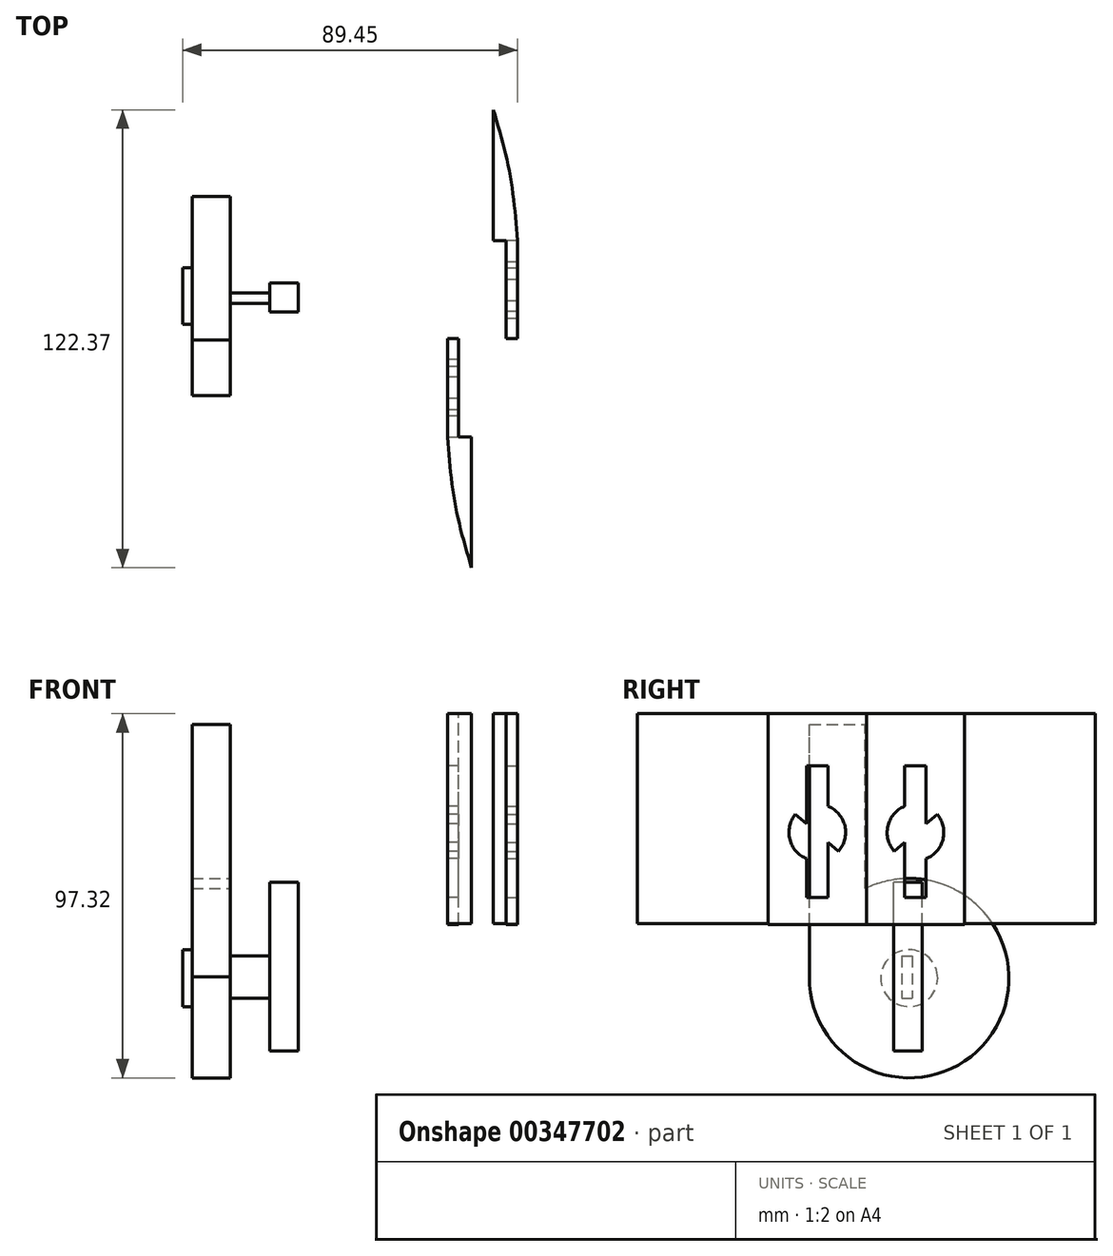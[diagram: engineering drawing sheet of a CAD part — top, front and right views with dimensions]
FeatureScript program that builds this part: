
annotation { "Feature Type Name" : "Feature", "Feature Type Description" : "" }
export const myFeature = defineFeature(function(context is Context, id is Id, definition is map)
    precondition{}
    {
        {
            var Q0;
            Q0=qCreatedBy(makeId("Right.planeOp"),FACE);
            var sketch = newSketch(context, id + "F0", { "sketchPlane" : qUnion([Q0])});
            skLineSegment(sketch, "E0.bottom", {"start": v(-13.16, -24.6) * mm, "end": v(13.1, -24.6) * mm});
            skLineSegment(sketch, "E0.top", {"start": v(-13.16, 31.74) * mm, "end": v(13.1, 31.74) * mm});
            skLineSegment(sketch, "E0.left", {"start": v(-13.16, -24.6) * mm, "end": v(-13.16, 31.74) * mm});
            skLineSegment(sketch, "E0.right", {"start": v(13.1, -24.6) * mm, "end": v(13.1, 31.74) * mm});
            skArc(sketch, "E1", {"start": v(5.65, -5.03) * mm, "mid": v(7.38, 1.69) * mm, "end": v(2.9, 6.99) * mm});
            skLineSegment(sketch, "E2.bottom", {"start": v(-2.85, -17.31) * mm, "end": v(2.9, -17.31) * mm});
            skLineSegment(sketch, "E2.top", {"start": v(-2.85, 17.78) * mm, "end": v(2.9, 17.78) * mm});
            skLineSegment(sketch, "E2.left", {"start": v(-2.85, -17.31) * mm, "end": v(-2.85, -7.01) * mm});
            skLineSegment(sketch, "E2.right", {"start": v(2.9, -17.31) * mm, "end": v(2.9, -2.58) * mm});
            skLineSegment(sketch, "E3", {"start": v(2.9, -2.58) * mm, "end": v(5.99, -5.32) * mm});
            skLineSegment(sketch, "E4", {"start": v(-2.85, 2.35) * mm, "end": v(-5.84, 4.82) * mm});
            skArc(sketch, "E5.trimOffspring", {"start": v(-5.84, 4.82) * mm, "mid": v(-7.34, -1.86) * mm, "end": v(-2.85, -7.01) * mm});
            skLineSegment(sketch, "E6.trimOffspring", {"start": v(2.9, 6.99) * mm, "end": v(2.9, 17.78) * mm});
            skLineSegment(sketch, "E7.trimOffspring", {"start": v(-2.85, 2.35) * mm, "end": v(-2.85, 17.78) * mm});
            skLineSegment(sketch, "E8.bottom", {"start": v(-49.36, -24.44) * mm, "end": v(-13.16, -24.44) * mm});
            skLineSegment(sketch, "E8.top", {"start": v(-49.36, 31.74) * mm, "end": v(-13.16, 31.74) * mm});
            skLineSegment(sketch, "E8.left", {"start": v(-49.36, -24.44) * mm, "end": v(-49.36, 31.74) * mm});
            skLineSegment(sketch, "E8.right", {"start": v(-13.16, -24.44) * mm, "end": v(-13.16, 31.74) * mm});
            skSolve(sketch);
        }
        {
            var Q0;
            Q0=makeQuery(id+"F0.imprint","IMPRINT",FACE,{"disambiguationData":[TD([[makeQuery(id+"F0.imprint","IMPRINT",EDGE,{"derivedFrom":sQuery(id+"F0.wireOp",EDGE,"E0.bottom")}),1.0]])]});
            extrude(context, id + "F1", {"entities" : qUnion([Q0]), "depth" : 3 * mm});
        }
        {
            var Q0;
            Q0=makeQuery(id+"F1.opExtrude","SWEPT_FACE",FACE,{"disambiguationData":[OSD([sQuery(id+"F0.wireOp",EDGE,"E0.top")])]});
            var sketch = newSketch(context, id + "F2", { "sketchPlane" : qUnion([Q0])});
            skLineSegment(sketch, "E9", {"start": v(0, -13.16) * mm, "end": v(6.43, -13.16) * mm});
            skLineSegment(sketch, "E10", {"start": v(6.43, -13.16) * mm, "end": v(6.43, -48.08) * mm});
            skFitSpline(sketch, "E11", {"points": [v(6.43, -48.08) * mm, v(2.07, -31.17) * mm, v(0, -13.16) * mm], "startDerivative": vector(-9.97, 33.75) * mm, "endDerivative": vector(-2.92, 36.08) * mm});
            skSolve(sketch);
        }
        {
            var Q0;
            Q0 = qSketchRegion(id + "F2", true);
            extrude(context, id + "F3", {"entities" : qUnion([Q0]), "operationType" : NewBodyOperationType.ADD, "oppositeDirection" : true, "depth" : 56.13 * mm});
        }
        {
            var Q0;
            Q0=makeQuery(id+"F1.opExtrude","SWEPT_BODY",BODY,{"disambiguationData":[OSD([sQuery(id+"F0.wireOp",EDGE,"E0.bottom"),sQuery(id+"F0.wireOp",EDGE,"E0.top"),sQuery(id+"F0.wireOp",EDGE,"E0.left"),sQuery(id+"F0.wireOp",EDGE,"E0.right"),sQuery(id+"F0.wireOp",EDGE,"E1"),sQuery(id+"F0.wireOp",EDGE,"E2.bottom"),sQuery(id+"F0.wireOp",EDGE,"E2.top"),sQuery(id+"F0.wireOp",EDGE,"E2.left"),sQuery(id+"F0.wireOp",EDGE,"E2.right"),sQuery(id+"F0.wireOp",EDGE,"E3"),sQuery(id+"F0.wireOp",EDGE,"E4"),sQuery(id+"F0.wireOp",EDGE,"E5.trimOffspring"),sQuery(id+"F0.wireOp",EDGE,"E6.trimOffspring"),sQuery(id+"F0.wireOp",EDGE,"E7.trimOffspring"),sQuery(id+"F0.wireOp",EDGE,"E8.right")])]});
            transform(context, id + "F4", {"entities" : qUnion([Q0]), "transformType" : TransformType.TRANSLATION_3D, "dx" : 0 * mm, "dy" : 63.5 * mm, "dz" : 2.54 * mm, "makeCopy" : true});
        }
        {
            var Q0;
            Q0=makeQuery(id+"F4.opPattern","COPY",BODY,{"derivedFrom":makeQuery(id+"F1.opExtrude","SWEPT_BODY",BODY,{"disambiguationData":[OSD([sQuery(id+"F0.wireOp",EDGE,"E0.bottom"),sQuery(id+"F0.wireOp",EDGE,"E0.top"),sQuery(id+"F0.wireOp",EDGE,"E0.left"),sQuery(id+"F0.wireOp",EDGE,"E0.right"),sQuery(id+"F0.wireOp",EDGE,"E1"),sQuery(id+"F0.wireOp",EDGE,"E2.bottom"),sQuery(id+"F0.wireOp",EDGE,"E2.top"),sQuery(id+"F0.wireOp",EDGE,"E2.left"),sQuery(id+"F0.wireOp",EDGE,"E2.right"),sQuery(id+"F0.wireOp",EDGE,"E3"),sQuery(id+"F0.wireOp",EDGE,"E4"),sQuery(id+"F0.wireOp",EDGE,"E5.trimOffspring"),sQuery(id+"F0.wireOp",EDGE,"E6.trimOffspring"),sQuery(id+"F0.wireOp",EDGE,"E7.trimOffspring"),sQuery(id+"F0.wireOp",EDGE,"E8.right")])]}),"instanceName":"1"});
            deleteBodies(context, id + "F5", {"entities" : qUnion([Q0])});
        }
        {
            var Q0;
            Q0=makeQuery(id+"F1.opExtrude","SWEPT_BODY",BODY,{"disambiguationData":[OSD([sQuery(id+"F0.wireOp",EDGE,"E0.bottom"),sQuery(id+"F0.wireOp",EDGE,"E0.top"),sQuery(id+"F0.wireOp",EDGE,"E0.left"),sQuery(id+"F0.wireOp",EDGE,"E0.right"),sQuery(id+"F0.wireOp",EDGE,"E1"),sQuery(id+"F0.wireOp",EDGE,"E2.bottom"),sQuery(id+"F0.wireOp",EDGE,"E2.top"),sQuery(id+"F0.wireOp",EDGE,"E2.left"),sQuery(id+"F0.wireOp",EDGE,"E2.right"),sQuery(id+"F0.wireOp",EDGE,"E3"),sQuery(id+"F0.wireOp",EDGE,"E4"),sQuery(id+"F0.wireOp",EDGE,"E5.trimOffspring"),sQuery(id+"F0.wireOp",EDGE,"E6.trimOffspring"),sQuery(id+"F0.wireOp",EDGE,"E7.trimOffspring"),sQuery(id+"F0.wireOp",EDGE,"E8.right")])]});
            var Q1;
            Q1=makeQuery(id+"F1.opExtrude","CAP_EDGE",EDGE,{"disambiguationData":[OSD([sQuery(id+"F0.wireOp",EDGE,"E0.right")])],"isStart":false});
            transform(context, id + "F6", {"entities" : qUnion([Q0]), "transformType" : TransformType.ROTATION, "transformAxis" : qUnion([Q1]), "angle" : 180 * degree, "makeCopy" : true});
        }
        {
            var Q0;
            Q0=makeQuery(id+"F6.opPattern","COPY",BODY,{"derivedFrom":makeQuery(id+"F1.opExtrude","SWEPT_BODY",BODY,{"disambiguationData":[OSD([sQuery(id+"F0.wireOp",EDGE,"E0.bottom"),sQuery(id+"F0.wireOp",EDGE,"E0.top"),sQuery(id+"F0.wireOp",EDGE,"E0.left"),sQuery(id+"F0.wireOp",EDGE,"E0.right"),sQuery(id+"F0.wireOp",EDGE,"E1"),sQuery(id+"F0.wireOp",EDGE,"E2.bottom"),sQuery(id+"F0.wireOp",EDGE,"E2.top"),sQuery(id+"F0.wireOp",EDGE,"E2.left"),sQuery(id+"F0.wireOp",EDGE,"E2.right"),sQuery(id+"F0.wireOp",EDGE,"E3"),sQuery(id+"F0.wireOp",EDGE,"E4"),sQuery(id+"F0.wireOp",EDGE,"E5.trimOffspring"),sQuery(id+"F0.wireOp",EDGE,"E6.trimOffspring"),sQuery(id+"F0.wireOp",EDGE,"E7.trimOffspring"),sQuery(id+"F0.wireOp",EDGE,"E8.right")])]}),"instanceName":"1"});
            transform(context, id + "F7", {"entities" : qUnion([Q0]), "transformType" : TransformType.TRANSLATION_3D, "dx" : 12.7 * mm, "dy" : 0 * mm, "dz" : 0 * mm, "makeCopy" : false});
        }
        {
            var Q0;
            Q0=qCreatedBy(makeId("Front.planeOp"),FACE);
            var sketch = newSketch(context, id + "F8", { "sketchPlane" : qUnion([Q0])});
            skLineSegment(sketch, "E12.bottom", {"start": v(-7.25, -33.05) * mm, "end": v(3.36, -33.05) * mm});
            skLineSegment(sketch, "E12.top", {"start": v(-7.25, -44.28) * mm, "end": v(3.36, -44.28) * mm});
            skLineSegment(sketch, "E12.left", {"start": v(-7.25, -33.05) * mm, "end": v(-7.25, -44.28) * mm});
            skLineSegment(sketch, "E12.right", {"start": v(3.36, -33.05) * mm, "end": v(3.36, -44.28) * mm});
            skSolve(sketch);
        }
        {
            var Q0;
            Q0 = qSketchRegion(id + "F8", true);
            extrude(context, id + "F9", {"entities" : qUnion([Q0]), "depth" : 2.8 * mm});
        }
        {
            var Q0;
            Q0=makeQuery(id+"F9.opExtrude","SWEPT_FACE",FACE,{"disambiguationData":[OSD([sQuery(id+"F8.wireOp",EDGE,"E12.left")])]});
            cPlane(context, id + "F10", {"entities" : qUnion([Q0]), "cplaneType" : CPlaneType.OFFSET, "offset" : 0 * mm, "width" : 152.4 * mm, "height" : 152.4 * mm});
        }
        {
            var Q0;
            Q0=qCreatedBy(id+"F10.planeOp",FACE);
            var sketch = newSketch(context, id + "F11", { "sketchPlane" : qUnion([Q0])});
            skCircle(sketch, "E13", {"center": v(0.85, -38.94) * mm, "radius": 7.6 * mm});
            skCircle(sketch, "E14", {"center": v(0.85, -38.94) * mm, "radius": 26.64 * mm});
            skLineSegment(sketch, "E15.top", {"start": v(27.5, 28.91) * mm, "end": v(12.57, 28.91) * mm});
            skLineSegment(sketch, "E15.left", {"start": v(27.5, -39.26) * mm, "end": v(27.5, 28.91) * mm});
            skLineSegment(sketch, "E15.right", {"start": v(12.57, -15.01) * mm, "end": v(12.57, 28.91) * mm});
            skSolve(sketch);
        }
        {
            var Q0;
            Q0=makeQuery(id+"F11.imprint","IMPRINT",FACE,{"disambiguationData":[TD([[makeQuery(id+"F11.imprint","IMPRINT",EDGE,{"derivedFrom":sQuery(id+"F11.wireOp",EDGE,"E13")}),1.0]])]});
            extrude(context, id + "F12", {"entities" : qUnion([Q0]), "operationType" : NewBodyOperationType.ADD, "depth" : 12.7 * mm});
        }
        {
            var Q0;
            Q0 = qSketchRegion(id + "F11", true);
            extrude(context, id + "F13", {"entities" : qUnion([Q0]), "operationType" : NewBodyOperationType.ADD, "depth" : 10.16 * mm});
        }
        {
            var Q0;
            Q0=makeQuery(id+"F9.opExtrude","SWEPT_FACE",FACE,{"disambiguationData":[OSD([sQuery(id+"F8.wireOp",EDGE,"E12.right")])]});
            var sketch = newSketch(context, id + "F14", { "sketchPlane" : qUnion([Q0])});
            skLineSegment(sketch, "E16.bottom", {"start": v(2.67, -58.4) * mm, "end": v(-5.06, -58.4) * mm});
            skLineSegment(sketch, "E16.top", {"start": v(2.67, -13.33) * mm, "end": v(-5.06, -13.33) * mm});
            skLineSegment(sketch, "E16.left", {"start": v(2.67, -58.4) * mm, "end": v(2.67, -13.33) * mm});
            skLineSegment(sketch, "E16.right", {"start": v(-5.06, -58.4) * mm, "end": v(-5.06, -13.33) * mm});
            skSolve(sketch);
        }
        {
            var Q0;
            Q0=makeQuery(id+"F9.opExtrude","SWEPT_BODY",BODY,{"disambiguationData":[OSD([sQuery(id+"F8.wireOp",EDGE,"E12.bottom"),sQuery(id+"F8.wireOp",EDGE,"E12.top"),sQuery(id+"F8.wireOp",EDGE,"E12.left"),sQuery(id+"F8.wireOp",EDGE,"E12.right")])]});
            transform(context, id + "F15", {"entities" : qUnion([Q0]), "transformType" : TransformType.TRANSLATION_3D, "dx" : -50.8 * mm, "dy" : 25.4 * mm, "dz" : 0 * mm, "makeCopy" : false});
        }
        {
            var Q0;
            Q0 = qSketchRegion(id + "F14", true);
            extrude(context, id + "F16", {"entities" : qUnion([Q0]), "depth" : 7.62 * mm});
        }
        {
            var Q0;
            Q0=makeQuery(id+"F16.opExtrude","SWEPT_BODY",BODY,{"disambiguationData":[OSD([sQuery(id+"F14.wireOp",EDGE,"E16.bottom"),sQuery(id+"F14.wireOp",EDGE,"E16.top"),sQuery(id+"F14.wireOp",EDGE,"E16.left"),sQuery(id+"F14.wireOp",EDGE,"E16.right")])]});
            transform(context, id + "F17", {"entities" : qUnion([Q0]), "transformType" : TransformType.TRANSLATION_3D, "dx" : -50.8 * mm, "dy" : 25.4 * mm, "dz" : 0 * mm, "makeCopy" : false});
        }
    });
